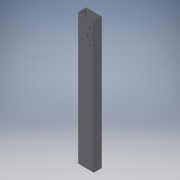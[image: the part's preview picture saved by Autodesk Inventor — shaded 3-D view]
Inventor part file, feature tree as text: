
AUTODESK INVENTOR PART (.ipt)
format: ipt  version: 2018 (Build 220112000, 112)  size: 131,584 bytes
history: native  units: in
note: dims shown in document units (in); Inventor stores cm internally (conversion verified against a paired STEP export)
features: extrude x3, sketch x3
ambient origin geometry x8: Origin, YZ Plane, XZ Plane, XY Plane, X Axis, Y Axis, Z Axis, Center Point
bodies: Solid1 (feature_tree)
feature tree (6):
  extrude  "Extrusion1"  Depth=1.0in
  extrude  "Extrusion2"  Depth=0.065in
  extrude  "Extrusion3"  Depth=0.065in
  sketch  "Sketch1"  dims[d0=2.0in d1=1.0in]
  sketch  "Sketch2"  dims[d2=0.065in d3=0.065in]
  sketch  "Sketch3"  dims[d4=0.065in d5=0.065in d6=17.0in d7=0.0in d8=0.2031in d9=0.5in d10=0.5in d11=0.5in d12=0.2031in d13=0.2031in d14=1.0in d15=2.0in d16=1.5in d17=24.0in d18=0.0in d19=0.75in d20=2.0in d21=1.0in d22=0.0in d26=1.0in]
